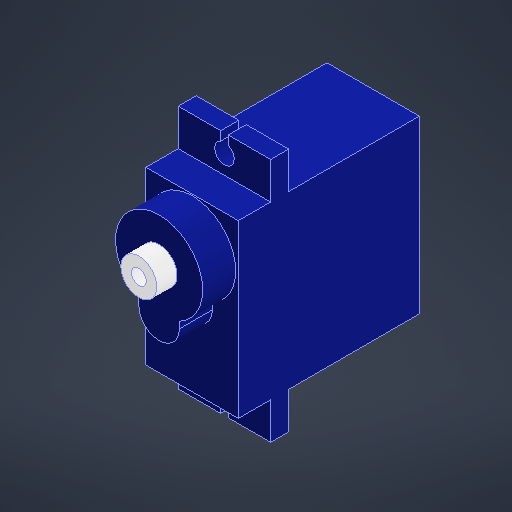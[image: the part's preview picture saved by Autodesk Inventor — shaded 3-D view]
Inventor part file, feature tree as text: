
AUTODESK INVENTOR PART (.ipt)
format: ipt  version: 2025.1 (Build 291241000, 241)  size: 344,576 bytes
history: native  units: mm
features: extrude x5, sketch x1
ambient origin geometry x8: Origin, YZ Plane, XZ Plane, XY Plane, X Axis, Y Axis, Z Axis, Center Point
bodies: Solid1 (feature_tree)
feature tree (6):
  sketch  "Sketch1"  dims[d0=22.8mm d1=12.3mm d2=4.9mm d3=4.9mm d4=2.6mm d5=2.5mm d6=1.0mm d7=4.9mm d8=2.5mm d9=1.0mm d10=2.6mm d11=4.9mm d12=11.6mm d14=6.0mm d15=2.0mm d16=4.8mm d17=5.4mm d18=6.0mm d19=5.8mm d20=17.4mm d21=0.0mm d22=2.4mm d23=0.0mm d24=4.3mm d25=0.0mm d26=4.4mm d27=0.0mm d28=2.7mm d29=0.0mm d38=0.5mm d39=0.872665mm d40=0.5mm d41=0.872665mm]
  extrude  "Extrusion1"  Depth=12.3mm
  extrude  "Extrusion2"  Depth=4.9mm
  extrude  "Extrusion3"  Depth=2.7mm
  extrude  "Extrusion4"  Depth=2.7mm
  extrude  "Extrusion5"  Depth=1.0mm
